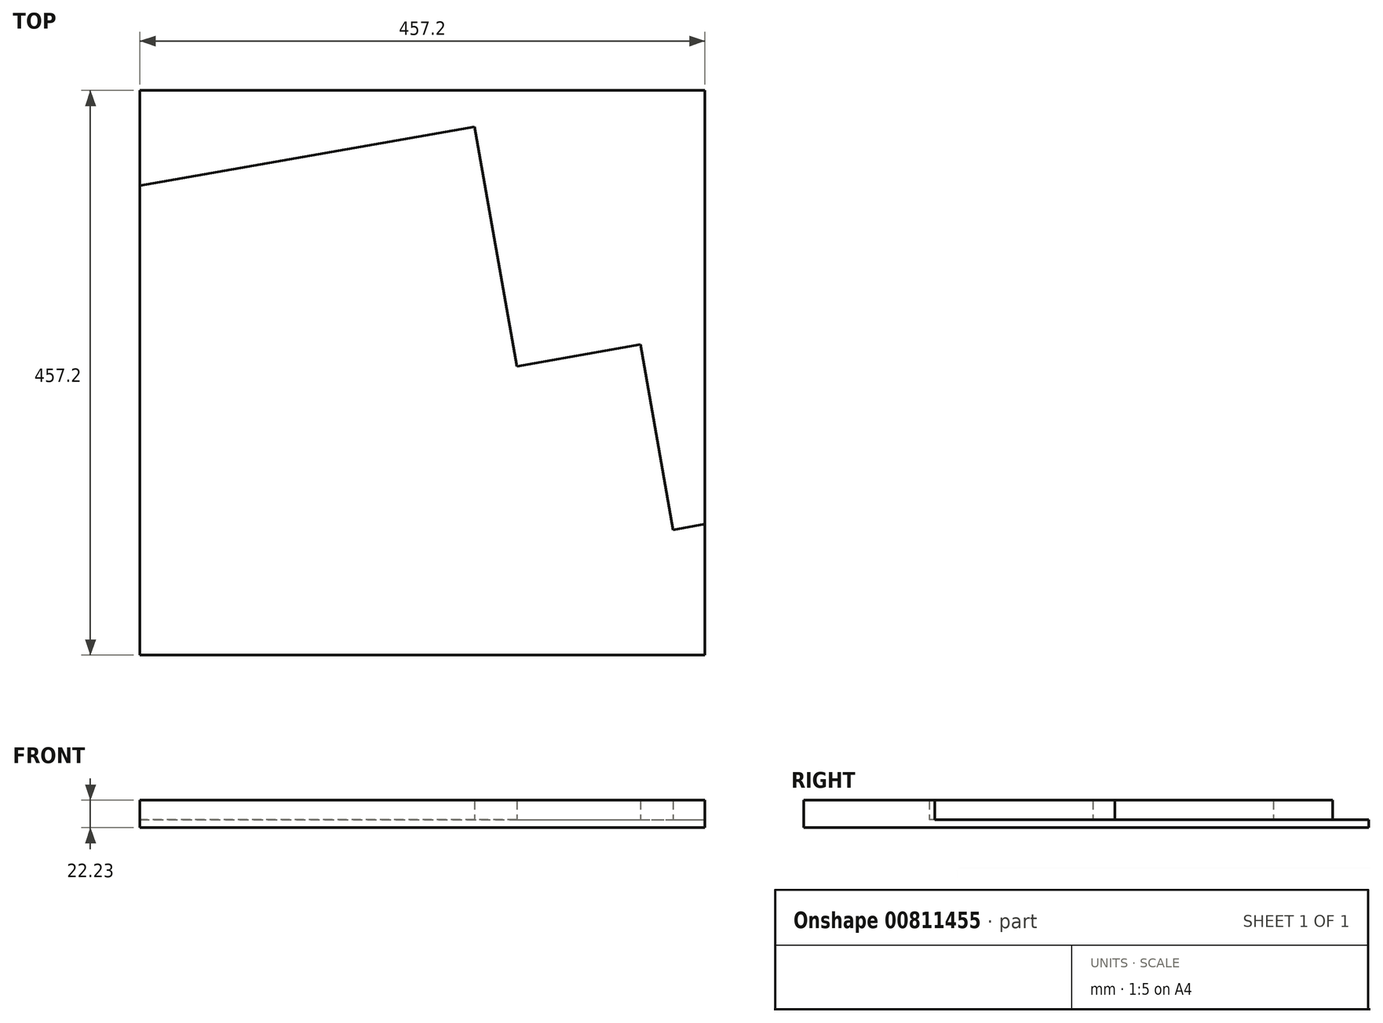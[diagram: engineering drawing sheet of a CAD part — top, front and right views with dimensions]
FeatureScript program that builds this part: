
annotation { "Feature Type Name" : "Feature", "Feature Type Description" : "" }
export const myFeature = defineFeature(function(context is Context, id is Id, definition is map)
    precondition{}
    {
        {
            var Q0;
            Q0=qCreatedBy(makeId("Top.planeOp"),FACE);
            var sketch = newSketch(context, id + "F0", { "sketchPlane" : qUnion([Q0])});
            skLineSegment(sketch, "E0.bottom", {"start": v(-228.6, 228.6) * mm, "end": v(228.6, 228.6) * mm});
            skLineSegment(sketch, "E0.top", {"start": v(-228.6, -228.6) * mm, "end": v(228.6, -228.6) * mm});
            skLineSegment(sketch, "E0.left", {"start": v(-228.6, 228.6) * mm, "end": v(-228.6, -228.6) * mm});
            skLineSegment(sketch, "E0.right", {"start": v(228.6, 228.6) * mm, "end": v(228.6, -228.6) * mm});
            skSolve(sketch);
        }
        {
            var Q0;
            Q0 = qSketchRegion(id + "F0", true);
            extrude(context, id + "F1", {"entities" : qUnion([Q0]), "depth" : 6.35 * mm, "offsetDistance" : 25.4 * mm});
        }
        {
            var Q0;
            Q0=makeQuery(id+"F1.opExtrude","CAP_FACE",FACE,{"disambiguationData":[OSD([sQuery(id+"F0.wireOp",EDGE,"E0.bottom"),sQuery(id+"F0.wireOp",EDGE,"E0.top"),sQuery(id+"F0.wireOp",EDGE,"E0.left"),sQuery(id+"F0.wireOp",EDGE,"E0.right")])],"isStart":false});
            var sketch = newSketch(context, id + "F2", { "sketchPlane" : qUnion([Q0])});
            skLineSegment(sketch, "E1", {"start": v(-228.6, -203.2) * mm, "end": v(228.6, -122.58) * mm});
            skLineSegment(sketch, "E2", {"start": v(228.6, -122.58) * mm, "end": v(228.6, -228.6) * mm});
            skLineSegment(sketch, "E3", {"start": v(228.6, -228.6) * mm, "end": v(-228.6, -228.6) * mm});
            skLineSegment(sketch, "E4", {"start": v(-228.6, -228.6) * mm, "end": v(-228.6, -203.2) * mm});
            skLineSegment(sketch, "E5", {"start": v(102.84, -144.76) * mm, "end": v(42.2, 199.19) * mm});
            skLineSegment(sketch, "E6", {"start": v(-228.6, -203.2) * mm, "end": v(-289.25, 140.74) * mm});
            skLineSegment(sketch, "E7", {"start": v(-289.25, 140.74) * mm, "end": v(42.2, 199.19) * mm});
            skLineSegment(sketch, "E8", {"start": v(76.37, 5.33) * mm, "end": v(176.43, 22.97) * mm});
            skLineSegment(sketch, "E9", {"start": v(176.43, 22.97) * mm, "end": v(202.9, -127.12) * mm});
            skSolve(sketch);
        }
        {
            var Q0;
            {var subQ4=sQuery(id+"F2.wireOp",EDGE,"E8");Q0=makeQuery(id+"F2.imprint","IMPRINT",FACE,{"disambiguationData":[TD([[makeQuery(id+"F2.imprint","IMPRINT",EDGE,{"derivedFrom":subQ4}),-1.0]])]});}
            extrude(context, id + "F3", {"entities" : qUnion([Q0]), "operationType" : NewBodyOperationType.ADD, "depth" : 15.88 * mm, "offsetDistance" : 25.4 * mm});
        }
        {
            var Q0;
            Q0=makeQuery(id+"F1.opExtrude","CAP_FACE",FACE,{"disambiguationData":[OSD([sQuery(id+"F0.wireOp",EDGE,"E0.bottom"),sQuery(id+"F0.wireOp",EDGE,"E0.top"),sQuery(id+"F0.wireOp",EDGE,"E0.left"),sQuery(id+"F0.wireOp",EDGE,"E0.right")])],"isStart":false});
            var sketch = newSketch(context, id + "F4", { "sketchPlane" : qUnion([Q0])});
            skLineSegment(sketch, "E10", {"start": v(202.9, -127.12) * mm, "end": v(-228.6, -203.2) * mm});
            skLineSegment(sketch, "E11", {"start": v(202.9, -127.12) * mm, "end": v(228.6, -122.58) * mm});
            skLineSegment(sketch, "E12", {"start": v(228.6, -122.58) * mm, "end": v(228.6, -228.6) * mm});
            skLineSegment(sketch, "E13", {"start": v(228.6, -228.6) * mm, "end": v(-228.6, -228.6) * mm});
            skLineSegment(sketch, "E14", {"start": v(-228.6, -228.6) * mm, "end": v(-228.6, -203.2) * mm});
            skSolve(sketch);
        }
        {
            var Q0;
            {var subQ0=sQuery(id+"F4.wireOp",EDGE,"E11");Q0=makeQuery(id+"F4.imprint","IMPRINT",FACE,{"disambiguationData":[TD([[makeQuery(id+"F4.imprint","IMPRINT",EDGE,{"derivedFrom":subQ0}),-1.0]])]});}
            extrude(context, id + "F5", {"entities" : qUnion([Q0]), "operationType" : NewBodyOperationType.ADD, "depth" : 15.88 * mm, "offsetDistance" : 25.4 * mm});
        }
        {
            var Q0;
            Q0=makeQuery(id+"F1.opExtrude","CAP_FACE",FACE,{"disambiguationData":[OSD([sQuery(id+"F0.wireOp",EDGE,"E0.bottom"),sQuery(id+"F0.wireOp",EDGE,"E0.top"),sQuery(id+"F0.wireOp",EDGE,"E0.left"),sQuery(id+"F0.wireOp",EDGE,"E0.right")])],"isStart":false});
            var sketch = newSketch(context, id + "F6", { "sketchPlane" : qUnion([Q0])});
            skLineSegment(sketch, "E15", {"start": v(102.84, -144.76) * mm, "end": v(42.2, 199.19) * mm});
            skLineSegment(sketch, "E16", {"start": v(42.2, 199.19) * mm, "end": v(-289.25, 140.74) * mm});
            skLineSegment(sketch, "E17", {"start": v(-289.25, 140.74) * mm, "end": v(-228.6, -203.2) * mm});
            skSolve(sketch);
        }
        {
            var Q0;
            Q0 = qSketchRegion(id + "F6", true);
            var Q1;
            {var subQ5=sQuery(id+"F6.wireOp",EDGE,"E15");var subQ9=makeQuery(id+"F6.imprint","INTERSECT",VERTEX,{"derivedFrom":[makeQuery(id+"F3.opExtrude","CAP_EDGE",EDGE,{"disambiguationData":[OSD([sQuery(id+"F2.wireOp",EDGE,"E8")])],"isStart":true}),subQ5]});Q1=makeQuery(id+"F6.imprint","IMPRINT",FACE,{"disambiguationData":[TD([[makeQuery(id+"F6.imprint","IMPRINT",EDGE,{"disambiguationData":[TD([[subQ9,-1.0]])],"derivedFrom":subQ5}),1.0]])]});}
            extrude(context, id + "F7", {"entities" : qUnion([Q0, Q1]), "operationType" : NewBodyOperationType.ADD, "depth" : 15.88 * mm, "offsetDistance" : 25.4 * mm});
        }
    });
